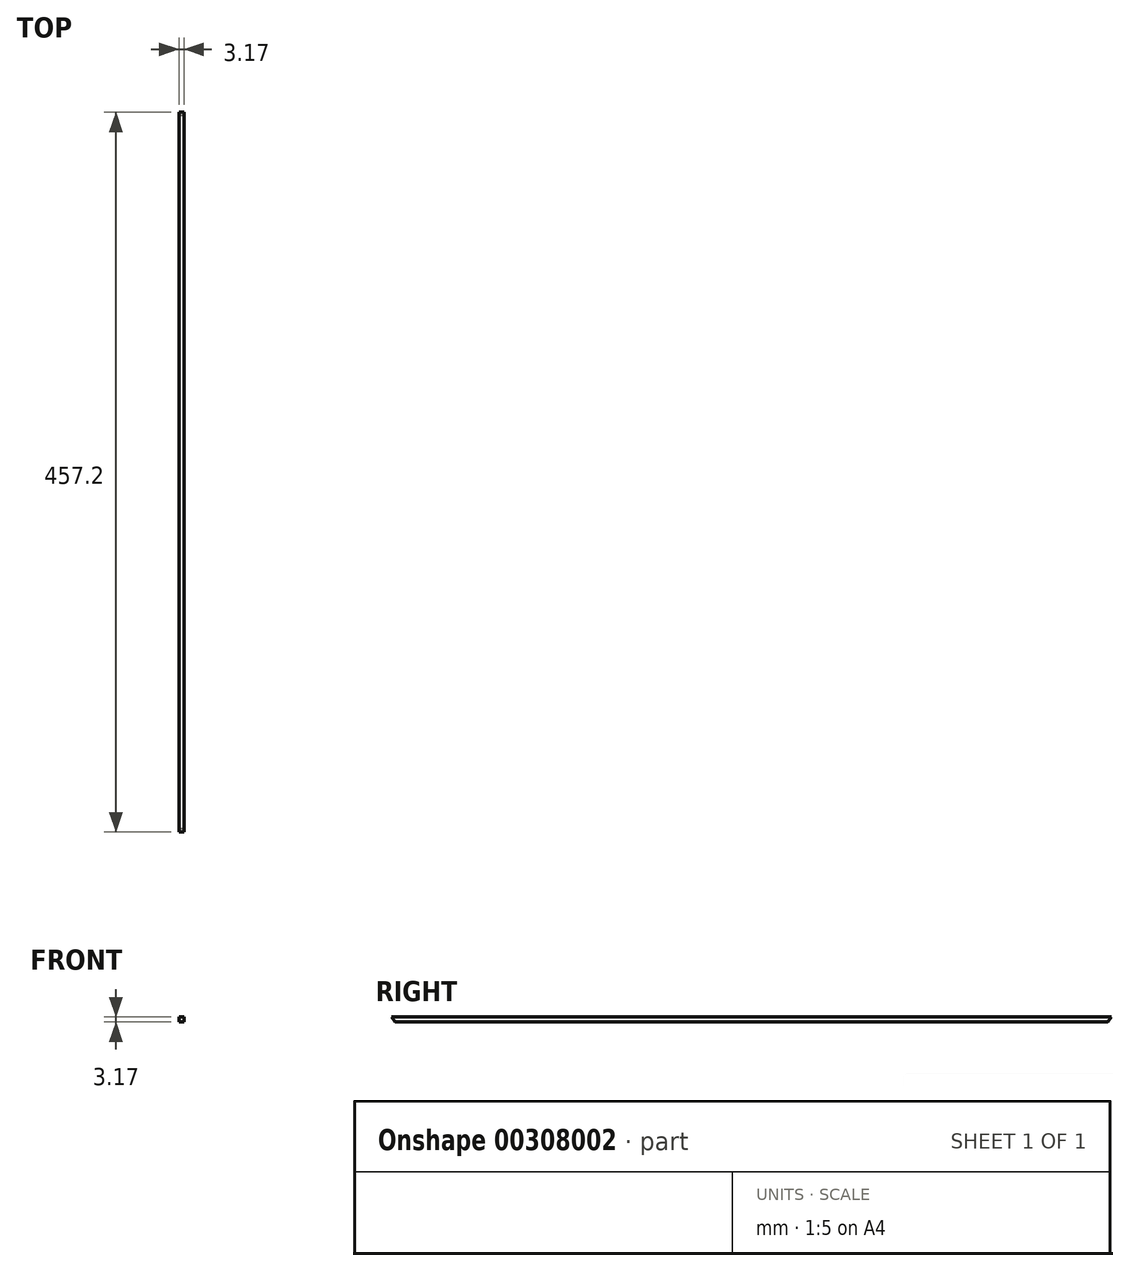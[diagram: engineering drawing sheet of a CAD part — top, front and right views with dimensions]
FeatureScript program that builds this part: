
annotation { "Feature Type Name" : "Feature", "Feature Type Description" : "" }
export const myFeature = defineFeature(function(context is Context, id is Id, definition is map)
    precondition{}
    {
        {
            var Q0;
            Q0=qCreatedBy(makeId("Right.planeOp"),FACE);
            var sketch = newSketch(context, id + "F0", { "sketchPlane" : qUnion([Q0])});
            skLineSegment(sketch, "E0", {"start": v(-228.6, 3.17) * mm, "end": v(0, 3.17) * mm});
            skLineSegment(sketch, "E1", {"start": v(0, 3.17) * mm, "end": v(228.6, 3.17) * mm});
            skLineSegment(sketch, "E2.2", {"start": v(-226.5, 0) * mm, "end": v(0, 0) * mm});
            skLineSegment(sketch, "E2.3", {"start": v(0, 0) * mm, "end": v(226.5, 0) * mm});
            skLineSegment(sketch, "E3", {"start": v(228.6, 3.18) * mm, "end": v(226.5, 0) * mm});
            skLineSegment(sketch, "E4", {"start": v(-228.6, 3.18) * mm, "end": v(-226.5, 0) * mm});
            skSolve(sketch);
        }
        {
            var Q0;
            Q0=makeQuery(id+"F0.imprint","IMPRINT",FACE,{"disambiguationData":[TD([[makeQuery(id+"F0.imprint","IMPRINT",EDGE,{"derivedFrom":sQuery(id+"F0.wireOp",EDGE,"E0")}),-1.0]])]});
            extrude(context, id + "F1", {"entities" : qUnion([Q0]), "depth" : 3.17 * mm});
        }
    });
